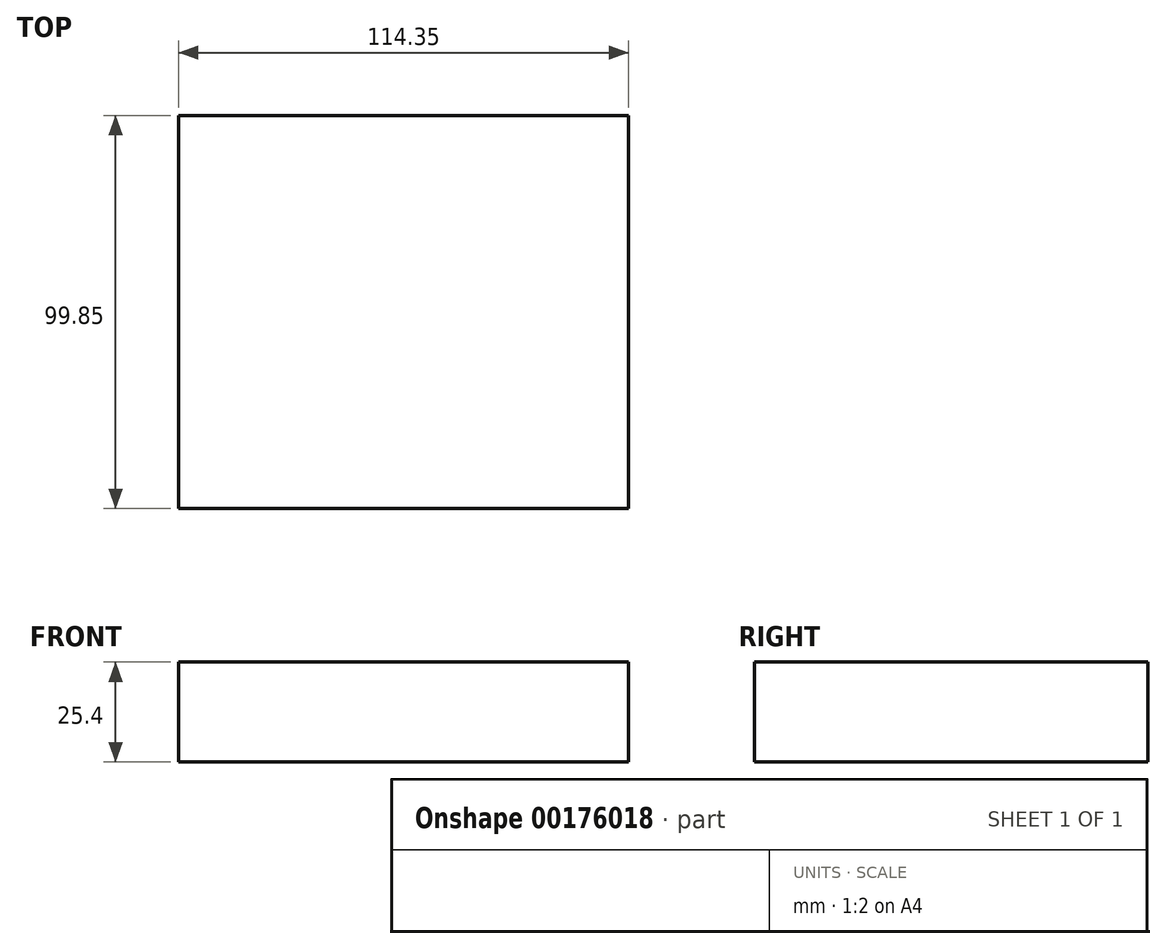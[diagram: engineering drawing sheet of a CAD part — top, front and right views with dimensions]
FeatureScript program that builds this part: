
annotation { "Feature Type Name" : "Feature", "Feature Type Description" : "" }
export const myFeature = defineFeature(function(context is Context, id is Id, definition is map)
    precondition{}
    {
        {
            var Q0;
            Q0=qCreatedBy(makeId("Top.planeOp"),FACE);
            var sketch = newSketch(context, id + "F0", { "sketchPlane" : qUnion([Q0])});
            skLineSegment(sketch, "E0.bottom", {"start": v(-191.16, 13.07) * mm, "end": v(-76.8, 13.07) * mm});
            skLineSegment(sketch, "E0.top", {"start": v(-191.16, -86.78) * mm, "end": v(-76.8, -86.78) * mm});
            skLineSegment(sketch, "E0.left", {"start": v(-191.16, 13.07) * mm, "end": v(-191.16, -86.78) * mm});
            skLineSegment(sketch, "E0.right", {"start": v(-76.8, 13.07) * mm, "end": v(-76.8, -86.78) * mm});
            skSolve(sketch);
        }
        {
            var Q0;
            Q0 = qSketchRegion(id + "F0", true);
            extrude(context, id + "F1", {"entities" : qUnion([Q0]), "depth" : 25.4 * mm});
        }
    });
